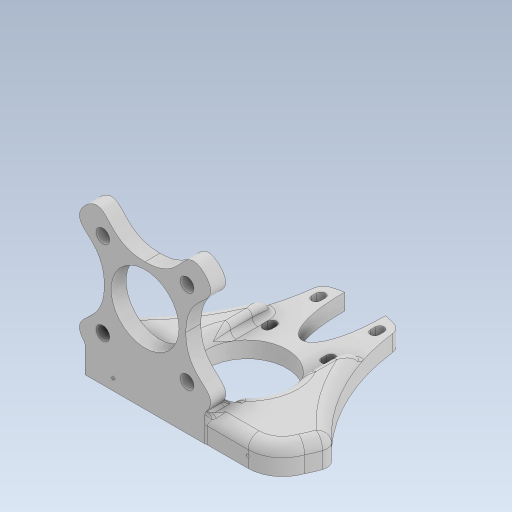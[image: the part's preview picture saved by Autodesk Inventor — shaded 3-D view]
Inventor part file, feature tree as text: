
AUTODESK INVENTOR PART (.ipt)
format: ipt  version: 2023 (Build 270158000, 158)  size: 1,921,536 bytes
history: native  units: in
note: dims shown in document units (in); Inventor stores cm internally (conversion verified against a paired STEP export)
features: sketch x7, extrude x6, fillet x4, plane x4, projected_geometry x4
ambient origin geometry x8: Origin, YZ Plane, XZ Plane, XY Plane, X Axis, Y Axis, Z Axis, Center Point
bodies: Solid1 (feature_tree)
feature tree (25):
  extrude  "Extrusion1"  Depth=0.3937in
  fillet  "Fillet2"  Radius=5.9055in
  plane  "Work Plane1"
  extrude  "Extrusion3"  Depth=0.5906in
  fillet  "Fillet3"  Radius=3.0187in
  extrude  "Extrusion4"  Depth=0.0098in
  plane  "Work Plane2"
  sketch  "Sketch7"  dims[d23=0.0394in d24=0.0394in d25=0.5592in d26=0.5592in]
  plane  "Work Plane4"
  extrude  "Extrusion9"  Depth=0.0787in TaperAngle=0.0deg
  extrude  "Extrusion12"  Depth=0.0394in
  fillet  "Fillet8"  Radius=0.5592in
  fillet  "Fillet9"  Radius=0.5592in
  extrude  "Extrusion5"  Depth=0.7067in TaperAngle=0.0deg
  sketch  "Sketch1"  dims[d5=0.3937in d6=0.0in d9=1.0in d13=5.9055in]
  sketch  "Sketch3"  dims[d14=0.1575in d15=0.5906in d16=3.0187in d17=0.0in]
  sketch  "Sketch4"  dims[d18=0.0787in d19=0.0098in]
  projected_geometry  "Projected Loop1"
  projected_geometry  "Projected Loop2"
  sketch  "Sketch5"  dims[d20=0.0098in d21=0.0787in d22=0.0in]
  projected_geometry  "Projected Loop3"
  plane  "Work Plane3"
  sketch  "Sketch9"  dims[d27=0.1575in d28=0.7067in d29=0.0in]
  sketch  "Sketch13"  dims[d32=1.7323in d33=1.5748in d34=0.1969in d35=0.7087in d36=0.5118in d46=90.0deg d47=1.1811in d48=1.5748in d49=1.2205in d50=1.2205in d51=0.1969in d52=1.5748in d54=360.0deg d56=0.9843in d57=1.7323in d60=0.2165in d61=0.0in d68=0.3937in d69=0.0787in d70=0.0in d71=0.0787in d72=0.0787in d73=0.7009in d74=0.1969in d75=0.1575in d76=0.315in d58=0.0197in d59=0.0344in]
  projected_geometry  "Projected Loop10"
